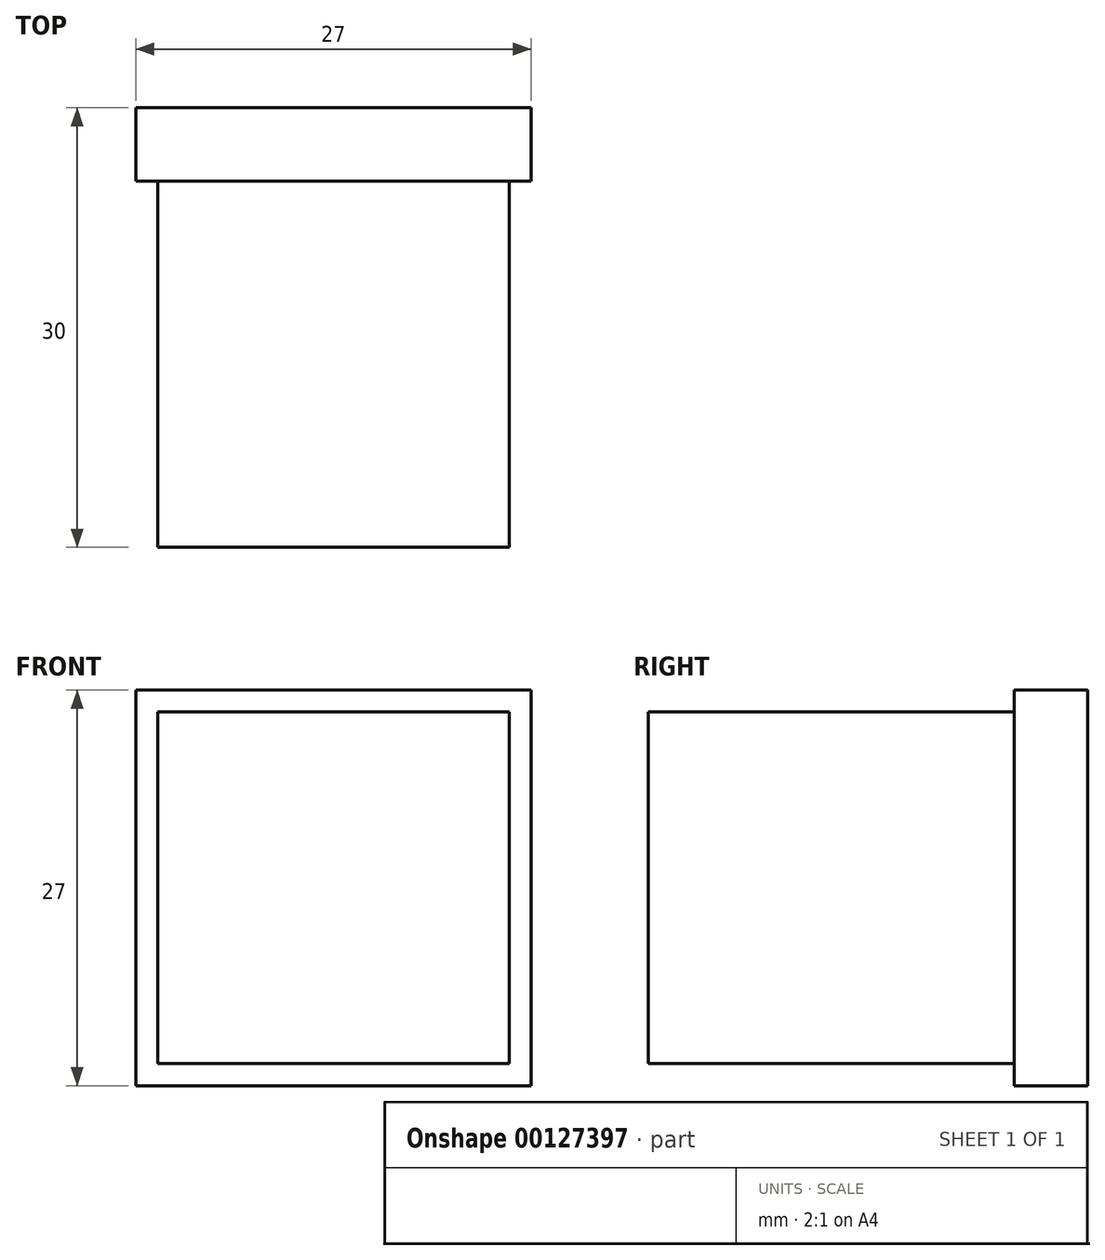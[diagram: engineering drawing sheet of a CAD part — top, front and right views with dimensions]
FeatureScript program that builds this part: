
annotation { "Feature Type Name" : "Feature", "Feature Type Description" : "" }
export const myFeature = defineFeature(function(context is Context, id is Id, definition is map)
    precondition{}
    {
        {
            var Q0;
            Q0=qCreatedBy(makeId("Front.planeOp"),FACE);
            var sketch = newSketch(context, id + "F0", { "sketchPlane" : qUnion([Q0])});
            skLineSegment(sketch, "E0.bottom", {"start": v(12, 12) * mm, "end": v(-12, 12) * mm});
            skLineSegment(sketch, "E0.top", {"start": v(12, -12) * mm, "end": v(-12, -12) * mm});
            skLineSegment(sketch, "E0.left", {"start": v(12, 12) * mm, "end": v(12, -12) * mm});
            skLineSegment(sketch, "E0.right", {"start": v(-12, 12) * mm, "end": v(-12, -12) * mm});
            skPoint(sketch, "E0.middle", {"position": v(0, 0) * mm});
            skSolve(sketch);
        }
        {
            var Q0;
            Q0=makeQuery(id+"F0.imprint","IMPRINT",FACE,{"disambiguationData":[TD([[makeQuery(id+"F0.imprint","IMPRINT",EDGE,{"derivedFrom":sQuery(id+"F0.wireOp",EDGE,"E0.bottom")}),1.0]])]});
            extrude(context, id + "F1", {"entities" : qUnion([Q0]), "depth" : 25 * mm});
        }
        {
            var Q0;
            Q0=qCreatedBy(makeId("Front.planeOp"),FACE);
            var sketch = newSketch(context, id + "F2", { "sketchPlane" : qUnion([Q0])});
            skLineSegment(sketch, "E1.bottom", {"start": v(-13.5, 13.5) * mm, "end": v(13.5, 13.5) * mm});
            skLineSegment(sketch, "E1.top", {"start": v(-13.5, -13.5) * mm, "end": v(13.5, -13.5) * mm});
            skLineSegment(sketch, "E1.left", {"start": v(-13.5, 13.5) * mm, "end": v(-13.5, -13.5) * mm});
            skLineSegment(sketch, "E1.right", {"start": v(13.5, 13.5) * mm, "end": v(13.5, -13.5) * mm});
            skPoint(sketch, "E1.middle", {"position": v(0, 0) * mm});
            skSolve(sketch);
        }
        {
            var Q0;
            Q0 = qSketchRegion(id + "F2", true);
            extrude(context, id + "F3", {"entities" : qUnion([Q0]), "operationType" : NewBodyOperationType.ADD, "oppositeDirection" : true, "depth" : 5 * mm});
        }
    });
